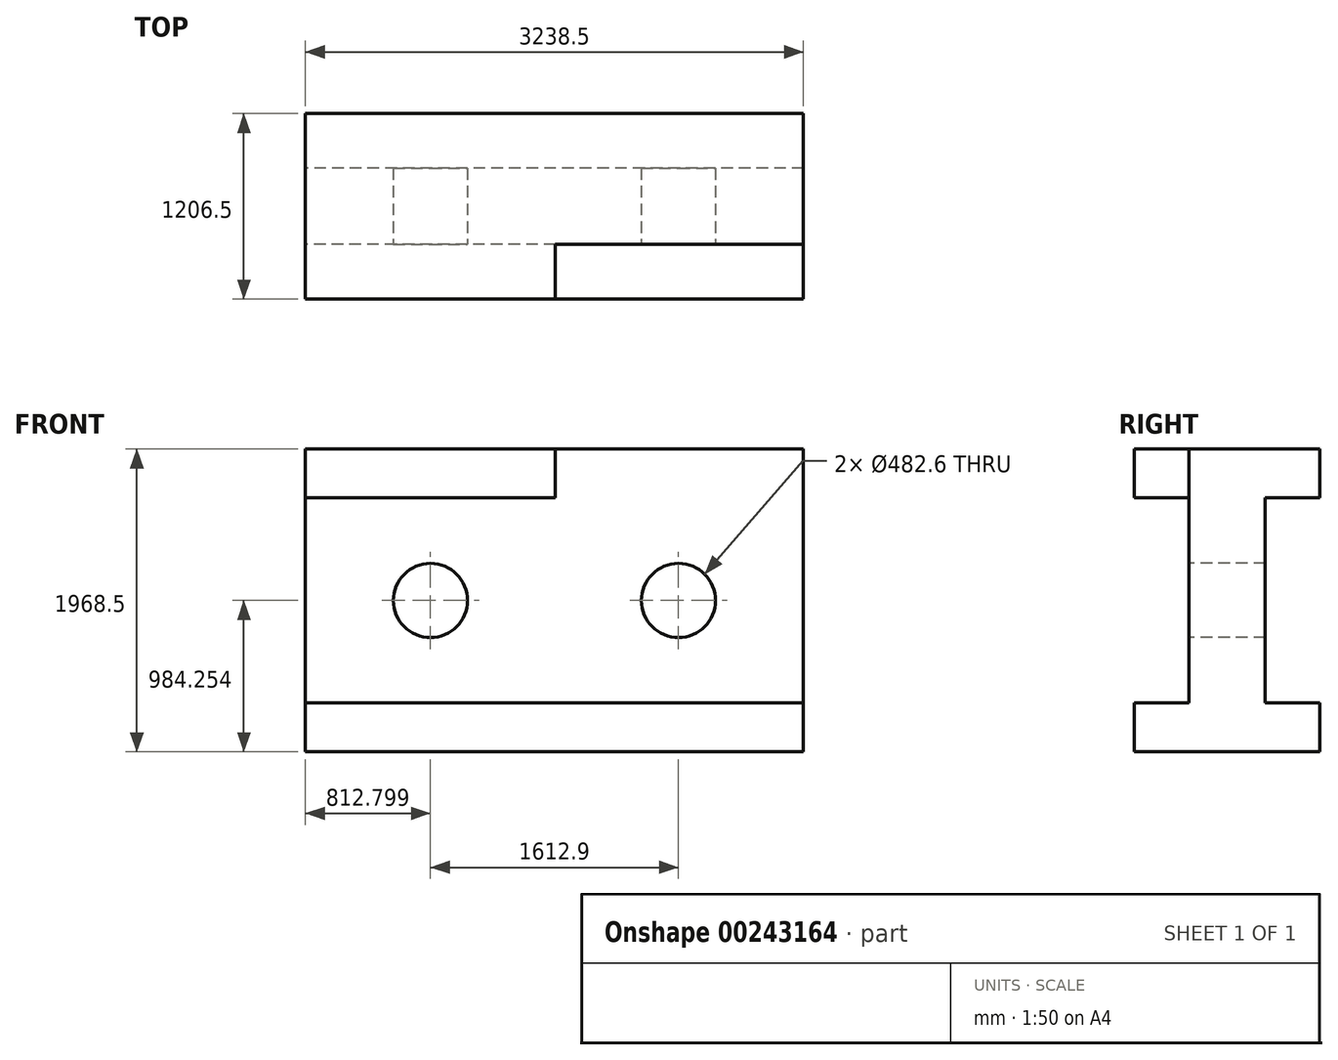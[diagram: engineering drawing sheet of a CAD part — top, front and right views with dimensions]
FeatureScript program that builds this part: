
annotation { "Feature Type Name" : "Feature", "Feature Type Description" : "" }
export const myFeature = defineFeature(function(context is Context, id is Id, definition is map)
    precondition{}
    {
        {
            var Q0;
            Q0=qCreatedBy(makeId("Front.planeOp"),FACE);
            var sketch = newSketch(context, id + "F0", { "sketchPlane" : qUnion([Q0])});
            skLineSegment(sketch, "E0", {"start": v(-1616.34, -177.53) * mm, "end": v(1622.16, -177.53) * mm});
            skLineSegment(sketch, "E1", {"start": v(1622.16, -177.53) * mm, "end": v(1622.16, 1790.97) * mm});
            skLineSegment(sketch, "E2", {"start": v(-1616.34, -177.53) * mm, "end": v(-1616.34, 1790.97) * mm});
            skLineSegment(sketch, "E3", {"start": v(-1616.34, 1790.97) * mm, "end": v(1622.16, 1790.97) * mm});
            skSolve(sketch);
        }
        {
            var Q0;
            Q0 = qSketchRegion(id + "F0", true);
            extrude(context, id + "F1", {"entities" : qUnion([Q0]), "depth" : 1206.5 * mm});
        }
        {
            var Q0;
            Q0=makeQuery(id+"F1.opExtrude","CAP_FACE",FACE,{"disambiguationData":[OSD([sQuery(id+"F0.wireOp",EDGE,"E0"),sQuery(id+"F0.wireOp",EDGE,"E1"),sQuery(id+"F0.wireOp",EDGE,"E2"),sQuery(id+"F0.wireOp",EDGE,"E3")])],"isStart":false});
            var sketch = newSketch(context, id + "F2", { "sketchPlane" : qUnion([Q0])});
            skLineSegment(sketch, "E4", {"start": v(1622.16, -177.53) * mm, "end": v(1622.16, 139.97) * mm});
            skLineSegment(sketch, "E5", {"start": v(1622.16, 139.97) * mm, "end": v(-1616.34, 139.97) * mm});
            skLineSegment(sketch, "E6", {"start": v(-1616.34, 1790.97) * mm, "end": v(-1616.34, 1473.47) * mm});
            skLineSegment(sketch, "E7", {"start": v(-1616.34, 1473.47) * mm, "end": v(-1616.34, 139.97) * mm});
            skLineSegment(sketch, "E8", {"start": v(1622.16, 1790.97) * mm, "end": v(9.26, 1790.97) * mm});
            skLineSegment(sketch, "E9", {"start": v(-1616.34, 1473.47) * mm, "end": v(9.26, 1473.47) * mm});
            skLineSegment(sketch, "E10", {"start": v(9.26, 1473.47) * mm, "end": v(9.26, 1790.97) * mm});
            skLineSegment(sketch, "E11", {"start": v(1622.16, 1790.97) * mm, "end": v(1622.16, 139.97) * mm});
            skSolve(sketch);
        }
        {
            var Q0;
            Q0 = qSketchRegion(id + "F2", true);
            extrude(context, id + "F3", {"entities" : qUnion([Q0]), "operationType" : NewBodyOperationType.REMOVE, "oppositeDirection" : true, "depth" : 355.6 * mm});
        }
        {
            var Q0;
            Q0=makeQuery(id+"F1.opExtrude","CAP_FACE",FACE,{"disambiguationData":[OSD([sQuery(id+"F0.wireOp",EDGE,"E0"),sQuery(id+"F0.wireOp",EDGE,"E1"),sQuery(id+"F0.wireOp",EDGE,"E2"),sQuery(id+"F0.wireOp",EDGE,"E3")])],"isStart":true});
            var sketch = newSketch(context, id + "F4", { "sketchPlane" : qUnion([Q0])});
            skLineSegment(sketch, "E12", {"start": v(-1622.16, 1790.97) * mm, "end": v(-1622.16, 1473.47) * mm});
            skLineSegment(sketch, "E13", {"start": v(-1622.16, -177.53) * mm, "end": v(-1622.16, 139.97) * mm});
            skLineSegment(sketch, "E14", {"start": v(-1622.16, 1473.47) * mm, "end": v(-1622.16, 139.97) * mm});
            skLineSegment(sketch, "E15", {"start": v(-1622.16, 1473.47) * mm, "end": v(1616.34, 1473.47) * mm});
            skLineSegment(sketch, "E16", {"start": v(-1622.16, 139.97) * mm, "end": v(1616.34, 139.97) * mm});
            skLineSegment(sketch, "E17", {"start": v(1616.34, 139.97) * mm, "end": v(1616.34, 1473.47) * mm});
            skSolve(sketch);
        }
        {
            var Q0;
            Q0 = qSketchRegion(id + "F4", true);
            extrude(context, id + "F5", {"entities" : qUnion([Q0]), "operationType" : NewBodyOperationType.REMOVE, "oppositeDirection" : true, "depth" : 355.6 * mm});
        }
        {
            var Q0;
            Q0=makeQuery(id+"F3.boolean.opBoolean","COPY",FACE,{"derivedFrom":makeQuery(id+"F3.opExtrude","CAP_FACE",FACE,{"disambiguationData":[OSD([sQuery(id+"F2.wireOp",EDGE,"E5"),sQuery(id+"F2.wireOp",EDGE,"E7"),sQuery(id+"F2.wireOp",EDGE,"E8"),sQuery(id+"F2.wireOp",EDGE,"E9"),sQuery(id+"F2.wireOp",EDGE,"E10"),sQuery(id+"F2.wireOp",EDGE,"E11")])],"isStart":false})});
            var sketch = newSketch(context, id + "F6", { "sketchPlane" : qUnion([Q0])});
            skLineSegment(sketch, "E18", {"start": v(9.26, 1473.47) * mm, "end": v(1622.16, 1473.47) * mm});
            skCircle(sketch, "E19", {"center": v(809.36, 806.72) * mm, "radius": 241.3 * mm});
            skCircle(sketch, "E20", {"center": v(-803.54, 806.72) * mm, "radius": 241.3 * mm});
            skSolve(sketch);
        }
        {
            var Q0;
            Q0 = qSketchRegion(id + "F6", true);
            extrude(context, id + "F7", {"entities" : qUnion([Q0]), "operationType" : NewBodyOperationType.REMOVE, "oppositeDirection" : true, "depth" : 495.3 * mm});
        }
    });
